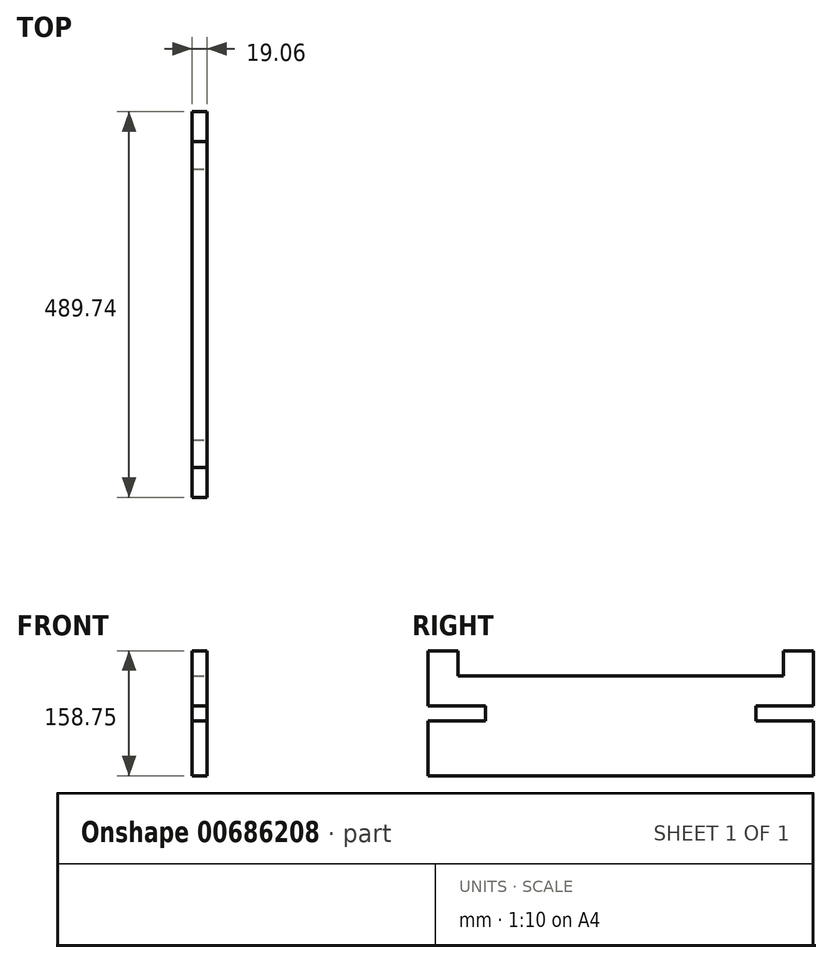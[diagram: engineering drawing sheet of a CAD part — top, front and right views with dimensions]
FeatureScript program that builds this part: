
annotation { "Feature Type Name" : "Feature", "Feature Type Description" : "" }
export const myFeature = defineFeature(function(context is Context, id is Id, definition is map)
    precondition{}
    {
        {
            var Q0;
            Q0=qCreatedBy(makeId("Front.planeOp"),FACE);
            var sketch = newSketch(context, id + "F0", { "sketchPlane" : qUnion([Q0])});
            skLineSegment(sketch, "E0.bottom", {"start": v(-9.53, 63.5) * mm, "end": v(9.53, 63.5) * mm});
            skLineSegment(sketch, "E0.top", {"start": v(-9.53, -63.5) * mm, "end": v(9.52, -63.5) * mm});
            skLineSegment(sketch, "E0.left", {"start": v(-9.53, 63.5) * mm, "end": v(-9.53, -63.5) * mm});
            skLineSegment(sketch, "E0.right", {"start": v(9.53, 63.5) * mm, "end": v(9.52, -63.5) * mm});
            skPoint(sketch, "E0.middle", {"position": v(0, 0) * mm});
            skSolve(sketch);
        }
        {
            var Q0;
            Q0 = qSketchRegion(id + "F0", true);
            extrude(context, id + "F1", {"entities" : qUnion([Q0]), "endBound" : BoundingType.SYMMETRIC, "depth" : 489.74 * mm, "offsetDistance" : 25.4 * mm});
        }
        {
            var Q0;
            Q0=makeQuery(id+"F1.opExtrude","SWEPT_FACE",FACE,{"disambiguationData":[OSD([sQuery(id+"F0.wireOp",EDGE,"E0.bottom")])]});
            var sketch = newSketch(context, id + "F2", { "sketchPlane" : qUnion([Q0])});
            skLineSegment(sketch, "E1.bottom", {"start": v(-9.53, 244.87) * mm, "end": v(9.53, 244.87) * mm});
            skLineSegment(sketch, "E1.top", {"start": v(-9.52, 206.77) * mm, "end": v(9.53, 206.77) * mm});
            skLineSegment(sketch, "E1.left", {"start": v(-9.53, 244.87) * mm, "end": v(-9.52, 206.77) * mm});
            skLineSegment(sketch, "E1.right", {"start": v(9.53, 244.87) * mm, "end": v(9.53, 206.77) * mm});
            skSolve(sketch);
        }
        {
            var Q0;
            Q0 = qSketchRegion(id + "F2", true);
            extrude(context, id + "F3", {"entities" : qUnion([Q0]), "depth" : 31.75 * mm, "offsetDistance" : 25.4 * mm});
        }
        {
            var Q0;
            Q0=makeQuery(id+"F3.opExtrude","SWEPT_BODY",BODY,{"disambiguationData":[OSD([sQuery(id+"F2.wireOp",EDGE,"E1.bottom"),sQuery(id+"F2.wireOp",EDGE,"E1.top"),sQuery(id+"F2.wireOp",EDGE,"E1.left"),sQuery(id+"F2.wireOp",EDGE,"E1.right")])]});
            var Q1;
            Q1=qCreatedBy(makeId("Front.planeOp"),FACE);
            mirror(context, id + "F4", {"operationType" : NewBodyOperationType.ADD, "entities" : qUnion([Q0]), "mirrorPlane" : qUnion([Q1])});
        }
        {
            var Q0;
            Q0=qCreatedBy(makeId("Right.planeOp"),FACE);
            var sketch = newSketch(context, id + "F5", { "sketchPlane" : qUnion([Q0])});
            skLineSegment(sketch, "E2", {"start": v(0, 95.25) * mm, "end": v(0, -63.5) * mm, "construction": true});
            skLineSegment(sketch, "E3", {"start": v(-216.3, 25.4) * mm, "end": v(-216.3, 6.35) * mm, "construction": true});
            skLineSegment(sketch, "E4", {"start": v(-216.3, 6.35) * mm, "end": v(-171.85, 6.35) * mm});
            skLineSegment(sketch, "E5", {"start": v(-171.85, 6.35) * mm, "end": v(-171.85, 25.4) * mm});
            skLineSegment(sketch, "E6", {"start": v(-171.85, 25.4) * mm, "end": v(-216.3, 25.4) * mm});
            skLineSegment(sketch, "E7", {"start": v(0, 15.88) * mm, "end": v(-171.85, 15.88) * mm, "construction": true});
            skLineSegment(sketch, "E8.MirrorCS", {"start": v(171.85, 25.4) * mm, "end": v(216.3, 25.4) * mm});
            skLineSegment(sketch, "E9.MirrorCS", {"start": v(216.3, 25.4) * mm, "end": v(216.3, 6.35) * mm, "construction": true});
            skLineSegment(sketch, "E10.MirrorCS", {"start": v(171.85, 6.35) * mm, "end": v(171.85, 25.4) * mm});
            skLineSegment(sketch, "E11.MirrorCS", {"start": v(216.3, 6.35) * mm, "end": v(171.85, 6.35) * mm});
            skLineSegment(sketch, "E12", {"start": v(-216.3, 25.4) * mm, "end": v(-244.87, 25.4) * mm});
            skLineSegment(sketch, "E13", {"start": v(-244.87, 25.4) * mm, "end": v(-244.87, 6.35) * mm});
            skLineSegment(sketch, "E14", {"start": v(-244.87, 6.35) * mm, "end": v(-216.3, 6.35) * mm});
            skLineSegment(sketch, "E15.MirrorCS", {"start": v(216.3, 25.4) * mm, "end": v(244.87, 25.4) * mm});
            skLineSegment(sketch, "E16.MirrorCS", {"start": v(244.87, 25.4) * mm, "end": v(244.87, 6.35) * mm});
            skLineSegment(sketch, "E17.MirrorCS", {"start": v(244.87, 6.35) * mm, "end": v(216.3, 6.35) * mm});
            skSolve(sketch);
        }
        {
            var Q0;
            Q0 = qSketchRegion(id + "F5", true);
            extrude(context, id + "F6", {"entities" : qUnion([Q0]), "operationType" : NewBodyOperationType.REMOVE, "endBound" : BoundingType.SYMMETRIC, "oppositeDirection" : true, "depth" : 25.4 * mm, "offsetDistance" : 25.4 * mm});
        }
    });
